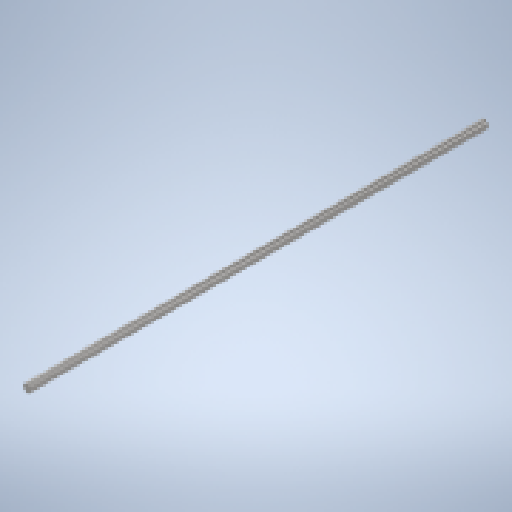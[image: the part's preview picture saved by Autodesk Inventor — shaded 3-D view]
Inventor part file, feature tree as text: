
AUTODESK INVENTOR PART (.ipt)
format: ipt  version: 2025.1 (Build 291241000, 241)  size: 136,704 bytes
history: native  units: mm
features: other x1, extrude x1
ambient origin geometry x8: Origin, YZ Plane, XZ Plane, XY Plane, X Axis, Y Axis, Z Axis, Center Point
bodies: Body1 (feature_tree)
feature tree (2):
  other  "Sólido1"
  extrude  "Extrusão1"  Depth=8.0mm
